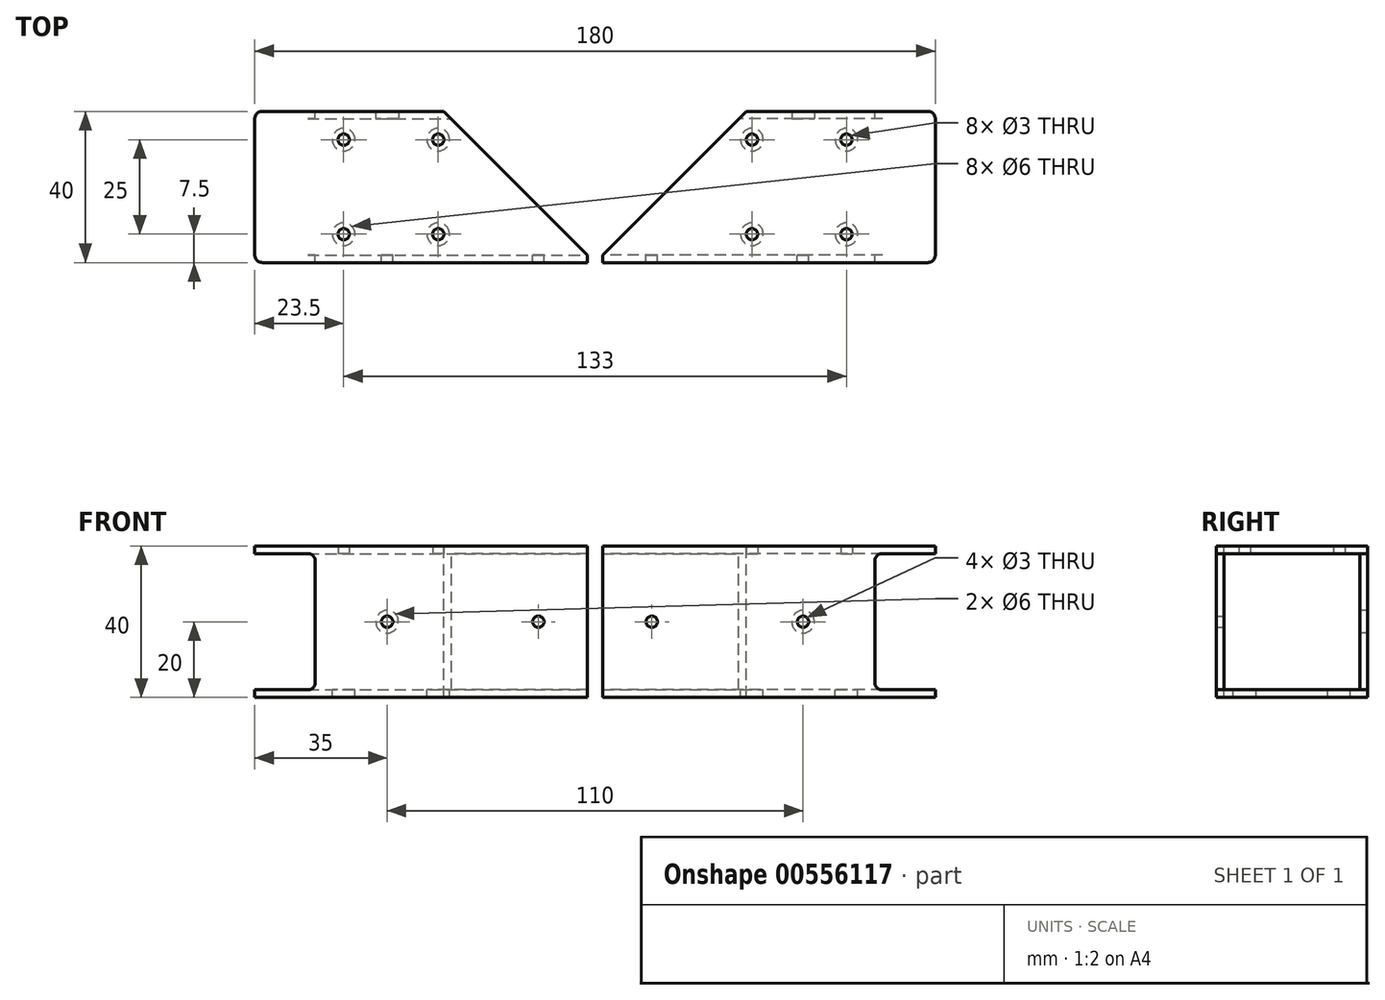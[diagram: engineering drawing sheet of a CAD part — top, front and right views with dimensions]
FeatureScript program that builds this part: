
annotation { "Feature Type Name" : "Feature", "Feature Type Description" : "" }
export const myFeature = defineFeature(function(context is Context, id is Id, definition is map)
    precondition{}
    {
        {
            var Q0;
            Q0=qCreatedBy(makeId("Right.planeOp"),FACE);
            var sketch = newSketch(context, id + "F0", { "sketchPlane" : qUnion([Q0])});
            skLineSegment(sketch, "E0.bottom", {"start": v(20, 20) * mm, "end": v(-20, 20) * mm});
            skLineSegment(sketch, "E0.top", {"start": v(20, -20) * mm, "end": v(-20, -20) * mm});
            skLineSegment(sketch, "E0.left", {"start": v(20, 20) * mm, "end": v(20, -20) * mm});
            skLineSegment(sketch, "E0.right", {"start": v(-20, 20) * mm, "end": v(-20, -20) * mm});
            skPoint(sketch, "E0.middle", {"position": v(0, 0) * mm});
            skSolve(sketch);
        }
        {
            var Q0;
            Q0=qSketchRegion(id+"F0",true);
            extrude(context, id + "F1", {"entities" : qUnion([Q0]), "oppositeDirection" : true, "depth" : 90 * mm, "offsetDistance" : 25 * mm});
        }
        {
            var Q0;
            Q0=makeQuery(id+"F1.opExtrude","CAP_FACE",FACE,{"disambiguationData":[OSD([sQuery(id+"F0.wireOp",EDGE,"E0.bottom"),sQuery(id+"F0.wireOp",EDGE,"E0.top"),sQuery(id+"F0.wireOp",EDGE,"E0.left"),sQuery(id+"F0.wireOp",EDGE,"E0.right")])],"isStart":false});
            var Q1;
            Q1=makeQuery(id+"F1.opExtrude","CAP_FACE",FACE,{"disambiguationData":[OSD([sQuery(id+"F0.wireOp",EDGE,"E0.bottom"),sQuery(id+"F0.wireOp",EDGE,"E0.top"),sQuery(id+"F0.wireOp",EDGE,"E0.left"),sQuery(id+"F0.wireOp",EDGE,"E0.right")])],"isStart":true});
            shell(context, id + "F2", {"entities" : qUnion([Q0, Q1]), "thickness" : 2 * mm});
        }
        {
            var Q0;
            Q0=makeQuery(id+"F2.opShell","OFFSET_FACE",FACE,{"disambiguationData":[OSD([sQuery(id+"F0.wireOp",EDGE,"E0.top")])]});
            var sketch = newSketch(context, id + "F3", { "sketchPlane" : qUnion([Q0])});
            skLineSegment(sketch, "E1", {"start": v(-90, 0) * mm, "end": v(0, 0) * mm, "construction": true});
            skLineSegment(sketch, "E2.bottom", {"start": v(-41.5, 12.5) * mm, "end": v(-66.5, 12.5) * mm, "construction": true});
            skLineSegment(sketch, "E2.top", {"start": v(-41.5, -12.5) * mm, "end": v(-66.5, -12.5) * mm, "construction": true});
            skLineSegment(sketch, "E2.left", {"start": v(-41.5, 12.5) * mm, "end": v(-41.5, -12.5) * mm, "construction": true});
            skLineSegment(sketch, "E2.right", {"start": v(-66.5, 12.5) * mm, "end": v(-66.5, -12.5) * mm, "construction": true});
            skPoint(sketch, "E2.middle", {"position": v(-54, 0) * mm});
            skLineSegment(sketch, "E3", {"start": v(-70, 18) * mm, "end": v(-70, -18) * mm, "construction": true});
            skSolve(sketch);
        }
        {
            var Q0;
            Q0=sQuery(id+"F3.wireOp",VERTEX,"E2.right.start");
            var Q1;
            Q1=sQuery(id+"F3.wireOp",VERTEX,"E2.bottom.start");
            var Q2;
            Q2=sQuery(id+"F3.wireOp",VERTEX,"E2.top.end");
            var Q3;
            Q3=sQuery(id+"F3.wireOp",VERTEX,"E2.left.end");
            var Q4;
            Q4=makeQuery(id+"F1.opExtrude","SWEPT_BODY",BODY,{"disambiguationData":[OSD([sQuery(id+"F0.wireOp",EDGE,"E0.bottom"),sQuery(id+"F0.wireOp",EDGE,"E0.top"),sQuery(id+"F0.wireOp",EDGE,"E0.left"),sQuery(id+"F0.wireOp",EDGE,"E0.right")])]});
            hole(context, id + "F4", {"style" : HoleStyle.SIMPLE, "endStyle" : HoleEndStyle.BLIND, "oppositeDirection" : true, "holeDiameter" : 3 * mm, "majorDiameter" : 5 * mm, "holeDepth" : 40 * mm, "isTappedThrough" : true, "tappedDepth" : 12 * mm, "tapClearance" : 3, "locations" : qUnion([Q0, Q1, Q2, Q3]), "scope" : qUnion([Q4])});
        }
        {
            var Q0;
            Q0=sQuery(id+"F3.wireOp",VERTEX,"E2.right.start");
            var Q1;
            Q1=sQuery(id+"F3.wireOp",VERTEX,"E2.top.end");
            var Q2;
            Q2=sQuery(id+"F3.wireOp",VERTEX,"E2.left.end");
            var Q3;
            Q3=sQuery(id+"F3.wireOp",VERTEX,"E2.left.start");
            var Q4;
            Q4=makeQuery(id+"F1.opExtrude","SWEPT_BODY",BODY,{"disambiguationData":[OSD([sQuery(id+"F0.wireOp",EDGE,"E0.bottom"),sQuery(id+"F0.wireOp",EDGE,"E0.top"),sQuery(id+"F0.wireOp",EDGE,"E0.left"),sQuery(id+"F0.wireOp",EDGE,"E0.right")])]});
            hole(context, id + "F5", {"style" : HoleStyle.SIMPLE, "endStyle" : HoleEndStyle.BLIND, "holeDiameter" : 6 * mm, "majorDiameter" : 5 * mm, "holeDepth" : 3 * mm, "isTappedThrough" : true, "tappedDepth" : 12 * mm, "tapClearance" : 3, "startFromSketch" : true, "locations" : qUnion([Q0, Q1, Q2, Q3]), "scope" : qUnion([Q4])});
        }
        {
            var Q0;
            Q0=makeQuery(id+"F1.opExtrude","SWEPT_FACE",FACE,{"disambiguationData":[OSD([sQuery(id+"F0.wireOp",EDGE,"E0.bottom")])]});
            var sketch = newSketch(context, id + "F6", { "sketchPlane" : qUnion([Q0])});
            skLineSegment(sketch, "E4", {"start": v(0, -20) * mm, "end": v(-40, 20) * mm});
            skLineSegment(sketch, "E5", {"start": v(-2, -20) * mm, "end": v(-2, -18) * mm});
            skSolve(sketch);
        }
        {
            var Q0;
            {var subQ1=sQuery(id+"F0.wireOp",EDGE,"E0.bottom");var subQ2=makeQuery(id+"F1.opExtrude","CAP_EDGE",EDGE,{"disambiguationData":[OSD([subQ1])],"isStart":true});Q0=makeQuery(id+"F6.imprint","IMPRINT",FACE,{"disambiguationData":[TD([[makeQuery(id+"F6.imprint","IMPRINT",EDGE,{"derivedFrom":subQ2}),-1.0]])]});}
            var Q1;
            {var subQ4=sQuery(id+"F6.wireOp",EDGE,"E5");Q1=makeQuery(id+"F6.imprint","IMPRINT",FACE,{"disambiguationData":[TD([[makeQuery(id+"F6.imprint","IMPRINT",EDGE,{"derivedFrom":subQ4}),-1.0]])]});}
            extrude(context, id + "F7", {"entities" : qUnion([Q0, Q1]), "operationType" : NewBodyOperationType.REMOVE, "endBound" : BoundingType.THROUGH_ALL, "oppositeDirection" : true, "depth" : 25 * mm, "offsetDistance" : 25 * mm});
        }
        {
            var Q0;
            Q0=makeQuery(id+"F2.opShell","OFFSET_FACE",FACE,{"disambiguationData":[OSD([sQuery(id+"F0.wireOp",EDGE,"E0.right")])]});
            var sketch = newSketch(context, id + "F8", { "sketchPlane" : qUnion([Q0])});
            skLineSegment(sketch, "E6", {"start": v(70, -20) * mm, "end": v(70, 20) * mm, "construction": true});
            skLineSegment(sketch, "E7", {"start": v(2, 0) * mm, "end": v(70, 0) * mm, "construction": true});
            skPoint(sketch, "E8", {"position": v(55, 0) * mm});
            skPoint(sketch, "E9", {"position": v(15, 0) * mm});
            skLineSegment(sketch, "E10.bottom", {"start": v(74, -18) * mm, "end": v(90, -18) * mm});
            skLineSegment(sketch, "E10.top", {"start": v(74, 18) * mm, "end": v(90, 18) * mm});
            skLineSegment(sketch, "E10.left", {"start": v(90, -18) * mm, "end": v(90, 18) * mm});
            skLineSegment(sketch, "E10.right", {"start": v(74, -18) * mm, "end": v(74, 18) * mm});
            skSolve(sketch);
        }
        {
            var Q0;
            Q0=makeQuery(id+"F8.imprint","IMPRINT",FACE,{"disambiguationData":[TD([[makeQuery(id+"F8.imprint","IMPRINT",EDGE,{"derivedFrom":sQuery(id+"F8.wireOp",EDGE,"E10.bottom")}),1.0]])]});
            var Q1;
            Q1=makeQuery(id+"F8.imprint","IMPRINT",FACE,{"disambiguationData":[TD([[makeQuery(id+"F8.imprint","IMPRINT",EDGE,{"derivedFrom":sQuery(id+"F8.wireOp",EDGE,"E10.bottom")}),-1.0]])]});
            extrude(context, id + "F9", {"entities" : qUnion([Q0, Q1]), "operationType" : NewBodyOperationType.REMOVE, "endBound" : BoundingType.THROUGH_ALL, "oppositeDirection" : true, "depth" : 25 * mm, "offsetDistance" : 25 * mm, "hasSecondDirection" : true, "secondDirectionBound" : SecondDirectionBoundingType.THROUGH_ALL, "secondDirectionOppositeDirection" : false, "secondDirectionDepth" : 25 * mm});
        }
        {
            var Q0;
            {var subQ0=sQuery(id+"F8.wireOp",EDGE,"E10.top");var subQ1=sQuery(id+"F0.wireOp",EDGE,"E0.right");var subQ2=sQuery(id+"F8.wireOp",EDGE,"E10.right");Q0=makeQuery(id+"F9.boolean.opBoolean","COPY",EDGE,{"disambiguationData":[TD([makeQuery(id+"F1.opExtrude","SWEPT_FACE",FACE,{"disambiguationData":[OSD([subQ1])]})])],"derivedFrom":makeQuery(id+"F9.opExtrude","SWEPT_EDGE",EDGE,{"disambiguationData":[OSD([subQ0,subQ2])]})});}
            var Q1;
            {var subQ0=sQuery(id+"F0.wireOp",EDGE,"E0.left");var subQ1=sQuery(id+"F8.wireOp",EDGE,"E10.top");var subQ2=sQuery(id+"F8.wireOp",EDGE,"E10.right");Q1=makeQuery(id+"F9.boolean.opBoolean","COPY",EDGE,{"disambiguationData":[TD([makeQuery(id+"F1.opExtrude","SWEPT_FACE",FACE,{"disambiguationData":[OSD([subQ0])]})])],"derivedFrom":makeQuery(id+"F9.opExtrude","SWEPT_EDGE",EDGE,{"disambiguationData":[OSD([subQ1,subQ2])]})});}
            var Q2;
            {var subQ0=sQuery(id+"F8.wireOp",EDGE,"E10.bottom");var subQ1=sQuery(id+"F0.wireOp",EDGE,"E0.left");var subQ2=sQuery(id+"F8.wireOp",EDGE,"E10.right");Q2=makeQuery(id+"F9.boolean.opBoolean","COPY",EDGE,{"disambiguationData":[TD([makeQuery(id+"F1.opExtrude","SWEPT_FACE",FACE,{"disambiguationData":[OSD([subQ1])]})])],"derivedFrom":makeQuery(id+"F9.opExtrude","SWEPT_EDGE",EDGE,{"disambiguationData":[OSD([subQ0,subQ2])]})});}
            var Q3;
            {var subQ0=sQuery(id+"F8.wireOp",EDGE,"E10.bottom");var subQ1=sQuery(id+"F0.wireOp",EDGE,"E0.right");var subQ2=sQuery(id+"F8.wireOp",EDGE,"E10.right");Q3=makeQuery(id+"F9.boolean.opBoolean","COPY",EDGE,{"disambiguationData":[TD([makeQuery(id+"F1.opExtrude","SWEPT_FACE",FACE,{"disambiguationData":[OSD([subQ1])]})])],"derivedFrom":makeQuery(id+"F9.opExtrude","SWEPT_EDGE",EDGE,{"disambiguationData":[OSD([subQ0,subQ2])]})});}
            var Q4;
            {var subQ0=sQuery(id+"F0.wireOp",EDGE,"E0.bottom");var subQ1=sQuery(id+"F0.wireOp",EDGE,"E0.left");Q4=makeQuery(id+"F9.boolean.opBoolean","SPLIT",EDGE,{"disambiguationData":[TD([makeQuery(id+"F1.opExtrude","SWEPT_FACE",FACE,{"disambiguationData":[OSD([subQ0])]})])],"derivedFrom":makeQuery(id+"F1.opExtrude","CAP_EDGE",EDGE,{"disambiguationData":[OSD([subQ1])],"isStart":false})});}
            var Q5;
            {var subQ0=sQuery(id+"F0.wireOp",EDGE,"E0.bottom");var subQ1=sQuery(id+"F0.wireOp",EDGE,"E0.right");Q5=makeQuery(id+"F9.boolean.opBoolean","SPLIT",EDGE,{"disambiguationData":[TD([makeQuery(id+"F1.opExtrude","SWEPT_FACE",FACE,{"disambiguationData":[OSD([subQ0])]})])],"derivedFrom":makeQuery(id+"F1.opExtrude","CAP_EDGE",EDGE,{"disambiguationData":[OSD([subQ1])],"isStart":false})});}
            var Q6;
            {var subQ0=sQuery(id+"F0.wireOp",EDGE,"E0.right");var subQ1=sQuery(id+"F0.wireOp",EDGE,"E0.top");Q6=makeQuery(id+"F9.boolean.opBoolean","SPLIT",EDGE,{"disambiguationData":[TD([makeQuery(id+"F1.opExtrude","SWEPT_FACE",FACE,{"disambiguationData":[OSD([subQ1])]})])],"derivedFrom":makeQuery(id+"F1.opExtrude","CAP_EDGE",EDGE,{"disambiguationData":[OSD([subQ0])],"isStart":false})});}
            var Q7;
            {var subQ0=sQuery(id+"F0.wireOp",EDGE,"E0.left");var subQ1=sQuery(id+"F0.wireOp",EDGE,"E0.top");Q7=makeQuery(id+"F9.boolean.opBoolean","SPLIT",EDGE,{"disambiguationData":[TD([makeQuery(id+"F1.opExtrude","SWEPT_FACE",FACE,{"disambiguationData":[OSD([subQ1])]})])],"derivedFrom":makeQuery(id+"F1.opExtrude","CAP_EDGE",EDGE,{"disambiguationData":[OSD([subQ0])],"isStart":false})});}
            fillet(context, id + "F10", {"entities" : qUnion([Q0, Q1, Q2, Q3, Q4, Q5, Q6, Q7]), "radius" : 2 * mm, "tangentPropagation" : true, "allowEdgeOverflow" : false});
        }
        {
            var Q0;
            Q0=sQuery(id+"F8.wireOp",VERTEX,"E8");
            var Q1;
            Q1=sQuery(id+"F8.wireOp",VERTEX,"E9");
            var Q2;
            Q2=makeQuery(id+"F1.opExtrude","SWEPT_BODY",BODY,{"disambiguationData":[OSD([sQuery(id+"F0.wireOp",EDGE,"E0.bottom"),sQuery(id+"F0.wireOp",EDGE,"E0.top"),sQuery(id+"F0.wireOp",EDGE,"E0.left"),sQuery(id+"F0.wireOp",EDGE,"E0.right")])]});
            hole(context, id + "F11", {"style" : HoleStyle.SIMPLE, "endStyle" : HoleEndStyle.BLIND, "holeDiameter" : 3 * mm, "majorDiameter" : 5 * mm, "holeDepth" : 3 * mm, "isTappedThrough" : true, "tappedDepth" : 12 * mm, "tapClearance" : 3, "startFromSketch" : true, "locations" : qUnion([Q0, Q1]), "scope" : qUnion([Q2])});
        }
        {
            var Q0;
            Q0=sQuery(id+"F8.wireOp",VERTEX,"E8");
            var Q1;
            Q1=makeQuery(id+"F1.opExtrude","SWEPT_BODY",BODY,{"disambiguationData":[OSD([sQuery(id+"F0.wireOp",EDGE,"E0.bottom"),sQuery(id+"F0.wireOp",EDGE,"E0.top"),sQuery(id+"F0.wireOp",EDGE,"E0.left"),sQuery(id+"F0.wireOp",EDGE,"E0.right")])]});
            hole(context, id + "F12", {"style" : HoleStyle.SIMPLE, "endStyle" : HoleEndStyle.BLIND, "oppositeDirection" : true, "holeDiameter" : 6 * mm, "majorDiameter" : 5 * mm, "holeDepth" : 40 * mm, "isTappedThrough" : true, "tappedDepth" : 12 * mm, "tapClearance" : 3, "startFromSketch" : true, "locations" : qUnion([Q0]), "scope" : qUnion([Q1])});
        }
        {
            var Q0;
            Q0=makeQuery(id+"F1.opExtrude","SWEPT_BODY",BODY,{"disambiguationData":[OSD([sQuery(id+"F0.wireOp",EDGE,"E0.bottom"),sQuery(id+"F0.wireOp",EDGE,"E0.top"),sQuery(id+"F0.wireOp",EDGE,"E0.left"),sQuery(id+"F0.wireOp",EDGE,"E0.right")])]});
            var Q1;
            Q1=qCreatedBy(makeId("Right.planeOp"),FACE);
            mirror(context, id + "F13", {"entities" : qUnion([Q0]), "mirrorPlane" : qUnion([Q1])});
        }
    });
